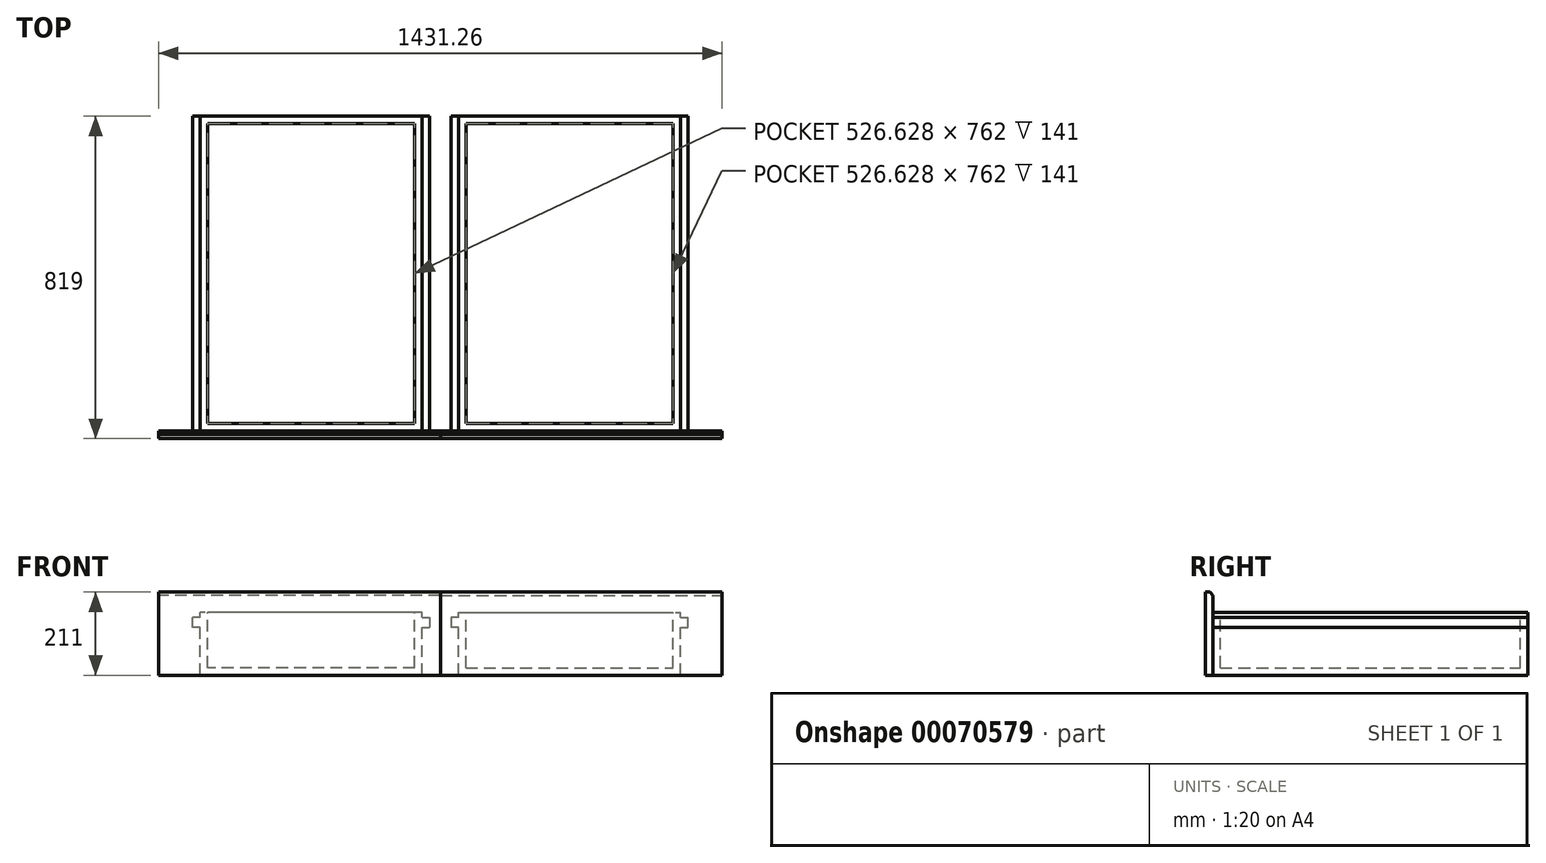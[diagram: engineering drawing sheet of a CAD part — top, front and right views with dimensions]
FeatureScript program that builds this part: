
annotation { "Feature Type Name" : "Feature", "Feature Type Description" : "" }
export const myFeature = defineFeature(function(context is Context, id is Id, definition is map)
    precondition{}
    {
        {
            var Q0;
            Q0=qCreatedBy(makeId("Front.planeOp"),FACE);
            var sketch = newSketch(context, id + "F0", { "sketchPlane" : qUnion([Q0])});
            skLineSegment(sketch, "E0.bottom", {"start": v(0, 0) * mm, "end": v(564.63, 0) * mm});
            skLineSegment(sketch, "E0.top", {"start": v(0, 160) * mm, "end": v(564.63, 160) * mm});
            skLineSegment(sketch, "E0.left", {"start": v(0, 0) * mm, "end": v(0, 160) * mm});
            skLineSegment(sketch, "E0.right", {"start": v(564.63, 0) * mm, "end": v(564.63, 160) * mm});
            skSolve(sketch);
        }
        {
            var Q0;
            Q0 = qSketchRegion(id + "F0", true);
            extrude(context, id + "F1", {"entities" : qUnion([Q0]), "depth" : 800 * mm});
        }
        {
            var Q0;
            Q0=makeQuery(id+"F1.opExtrude","SWEPT_FACE",FACE,{"disambiguationData":[OSD([sQuery(id+"F0.wireOp",EDGE,"E0.top")])]});
            shell(context, id + "F2", {"entities" : qUnion([Q0]), "thickness" : 19 * mm});
        }
        {
            var Q0;
            Q0=makeQuery(id+"F1.opExtrude","CAP_FACE",FACE,{"disambiguationData":[OSD([sQuery(id+"F0.wireOp",EDGE,"E0.bottom"),sQuery(id+"F0.wireOp",EDGE,"E0.top"),sQuery(id+"F0.wireOp",EDGE,"E0.left"),sQuery(id+"F0.wireOp",EDGE,"E0.right")])],"isStart":false});
            var sketch = newSketch(context, id + "F3", { "sketchPlane" : qUnion([Q0])});
            skLineSegment(sketch, "E1.bottom", {"start": v(0, 147) * mm, "end": v(-19, 147) * mm});
            skLineSegment(sketch, "E1.top", {"start": v(0, 122) * mm, "end": v(-19, 122) * mm});
            skLineSegment(sketch, "E1.left", {"start": v(0, 147) * mm, "end": v(0, 122) * mm});
            skLineSegment(sketch, "E1.right", {"start": v(-19, 147) * mm, "end": v(-19, 122) * mm});
            skLineSegment(sketch, "E2.bottom", {"start": v(564.63, 122) * mm, "end": v(583.63, 122) * mm});
            skLineSegment(sketch, "E2.top", {"start": v(564.63, 147) * mm, "end": v(583.63, 147) * mm});
            skLineSegment(sketch, "E2.left", {"start": v(564.63, 122) * mm, "end": v(564.63, 147) * mm});
            skLineSegment(sketch, "E2.right", {"start": v(583.63, 122) * mm, "end": v(583.63, 147) * mm});
            skSolve(sketch);
        }
        {
            var Q0;
            Q0 = qSketchRegion(id + "F3", true);
            extrude(context, id + "F4", {"entities" : qUnion([Q0]), "oppositeDirection" : true, "depth" : 800 * mm});
        }
        {
            var Q0;
            Q0=makeQuery(id+"F1.opExtrude","SWEPT_BODY",BODY,{"disambiguationData":[OSD([sQuery(id+"F0.wireOp",EDGE,"E0.bottom"),sQuery(id+"F0.wireOp",EDGE,"E0.top"),sQuery(id+"F0.wireOp",EDGE,"E0.left"),sQuery(id+"F0.wireOp",EDGE,"E0.right")])]});
            var Q1;
            Q1=makeQuery(id+"F4.opExtrude","SWEPT_BODY",BODY,{"disambiguationData":[OSD([sQuery(id+"F3.wireOp",EDGE,"E1.bottom"),sQuery(id+"F3.wireOp",EDGE,"E1.top"),sQuery(id+"F3.wireOp",EDGE,"E1.left"),sQuery(id+"F3.wireOp",EDGE,"E1.right")])]});
            var Q2;
            Q2=makeQuery(id+"F4.opExtrude","SWEPT_BODY",BODY,{"disambiguationData":[OSD([sQuery(id+"F3.wireOp",EDGE,"E2.bottom"),sQuery(id+"F3.wireOp",EDGE,"E2.top"),sQuery(id+"F3.wireOp",EDGE,"E2.left"),sQuery(id+"F3.wireOp",EDGE,"E2.right")])]});
            booleanBodies(context, id + "F5", {"operationType" : BooleanOperationType.UNION, "tools" : qUnion([Q0, Q1, Q2])});
        }
        {
            var Q0;
            Q0=makeQuery(id+"F5.opBoolean","MERGE",FACE,{"derivedFrom":[makeQuery(id+"F1.opExtrude","CAP_FACE",FACE,{"disambiguationData":[OSD([sQuery(id+"F0.wireOp",EDGE,"E0.bottom"),sQuery(id+"F0.wireOp",EDGE,"E0.top"),sQuery(id+"F0.wireOp",EDGE,"E0.left"),sQuery(id+"F0.wireOp",EDGE,"E0.right")])],"isStart":false}),makeQuery(id+"F4.opExtrude","CAP_FACE",FACE,{"disambiguationData":[OSD([sQuery(id+"F3.wireOp",EDGE,"E1.bottom"),sQuery(id+"F3.wireOp",EDGE,"E1.top"),sQuery(id+"F3.wireOp",EDGE,"E1.left"),sQuery(id+"F3.wireOp",EDGE,"E1.right")])],"isStart":true}),makeQuery(id+"F4.opExtrude","CAP_FACE",FACE,{"disambiguationData":[OSD([sQuery(id+"F3.wireOp",EDGE,"E2.bottom"),sQuery(id+"F3.wireOp",EDGE,"E2.top"),sQuery(id+"F3.wireOp",EDGE,"E2.left"),sQuery(id+"F3.wireOp",EDGE,"E2.right")])],"isStart":true})]});
            var sketch = newSketch(context, id + "F6", { "sketchPlane" : qUnion([Q0])});
            skLineSegment(sketch, "E3.bottom", {"start": v(-46, 0) * mm, "end": v(669.63, 0) * mm});
            skLineSegment(sketch, "E3.top", {"start": v(-46, 211) * mm, "end": v(669.63, 211) * mm});
            skLineSegment(sketch, "E3.left", {"start": v(-46, 0) * mm, "end": v(-46, 211) * mm});
            skLineSegment(sketch, "E3.right", {"start": v(669.63, 0) * mm, "end": v(669.63, 211) * mm});
            skSolve(sketch);
        }
        {
            var Q0;
            Q0 = qSketchRegion(id + "F6", true);
            extrude(context, id + "F7", {"entities" : qUnion([Q0]), "operationType" : NewBodyOperationType.ADD, "depth" : 19 * mm});
        }
        {
            var Q0;
            Q0=makeQuery(id+"F7.opExtrude","CAP_FACE",FACE,{"disambiguationData":[OSD([sQuery(id+"F6.wireOp",EDGE,"E3.bottom"),sQuery(id+"F6.wireOp",EDGE,"E3.top"),sQuery(id+"F6.wireOp",EDGE,"E3.left"),sQuery(id+"F6.wireOp",EDGE,"E3.right")])],"isStart":false});
            var sketch = newSketch(context, id + "F8", { "sketchPlane" : qUnion([Q0])});
            skLineSegment(sketch, "E4.bottom", {"start": v(-46, 211) * mm, "end": v(114, 211) * mm});
            skLineSegment(sketch, "E4.top", {"start": v(-46, 171) * mm, "end": v(114, 171) * mm});
            skLineSegment(sketch, "E4.left", {"start": v(-46, 211) * mm, "end": v(-46, 171) * mm});
            skLineSegment(sketch, "E4.right", {"start": v(114, 211) * mm, "end": v(114, 171) * mm});
            skSolve(sketch);
        }
        {
            var Q0;
            Q0=makeQuery(id+"F7.opExtrude","CAP_EDGE",EDGE,{"disambiguationData":[OSD([sQuery(id+"F6.wireOp",EDGE,"E3.top")])],"isStart":true});
            chamfer(context, id + "F9", {"entities" : qUnion([Q0]), "width" : 8 * mm, "tangentPropagation" : true});
        }
        {
            var Q0;
            Q0=makeQuery(id+"F1.opExtrude","SWEPT_BODY",BODY,{"disambiguationData":[OSD([sQuery(id+"F0.wireOp",EDGE,"E0.bottom"),sQuery(id+"F0.wireOp",EDGE,"E0.top"),sQuery(id+"F0.wireOp",EDGE,"E0.left"),sQuery(id+"F0.wireOp",EDGE,"E0.right")])]});
            var Q1;
            Q1=makeQuery(id+"F7.opExtrude","SWEPT_FACE",FACE,{"disambiguationData":[OSD([sQuery(id+"F6.wireOp",EDGE,"E3.left")])]});
            mirror(context, id + "F10", {"entities" : qUnion([Q0]), "mirrorPlane" : qUnion([Q1])});
        }
    });
